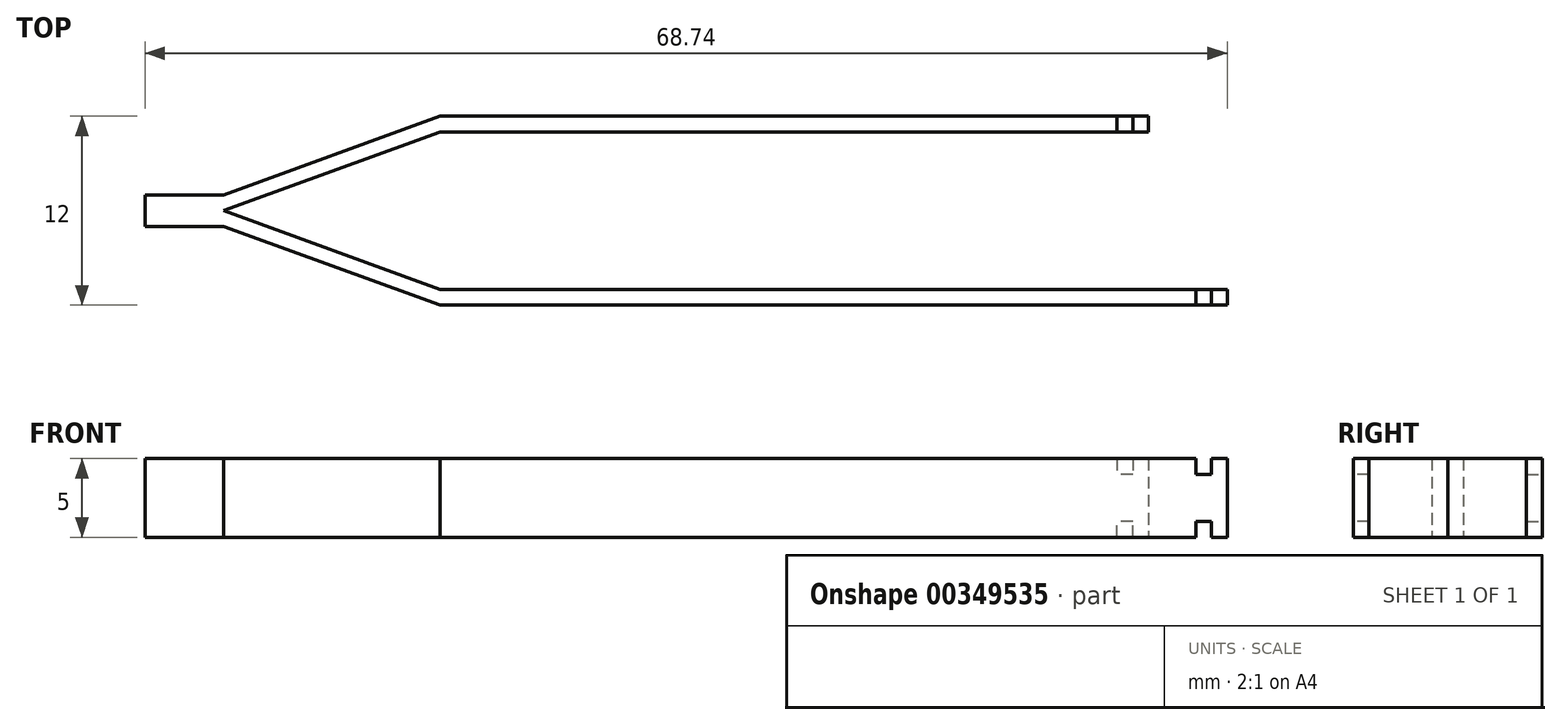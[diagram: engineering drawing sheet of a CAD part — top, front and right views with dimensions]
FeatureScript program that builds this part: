
annotation { "Feature Type Name" : "Feature", "Feature Type Description" : "" }
export const myFeature = defineFeature(function(context is Context, id is Id, definition is map)
    precondition{}
    {
        {
            var Q0;
            Q0=qCreatedBy(makeId("Top.planeOp"),FACE);
            var sketch = newSketch(context, id + "F0", { "sketchPlane" : qUnion([Q0])});
            skLineSegment(sketch, "E0", {"start": v(0, 0) * mm, "end": v(43.22, 0) * mm, "construction": true});
            skLineSegment(sketch, "E1", {"start": v(0, 0) * mm, "end": v(13.74, -5) * mm});
            skLineSegment(sketch, "E2", {"start": v(13.74, -5) * mm, "end": v(63.74, -5) * mm});
            skLineSegment(sketch, "E3", {"start": v(63.74, -5) * mm, "end": v(63.74, -6) * mm});
            skLineSegment(sketch, "E4", {"start": v(63.74, -6) * mm, "end": v(13.74, -6) * mm});
            skLineSegment(sketch, "E5", {"start": v(13.74, -6) * mm, "end": v(0, -1) * mm});
            skLineSegment(sketch, "E6", {"start": v(0, -1) * mm, "end": v(-5, -1) * mm});
            skLineSegment(sketch, "E7", {"start": v(-5, 1) * mm, "end": v(-5, -1) * mm});
            skLineSegment(sketch, "E8", {"start": v(-5, 1) * mm, "end": v(0, 1) * mm});
            skLineSegment(sketch, "E9", {"start": v(0, 1) * mm, "end": v(13.74, 6) * mm});
            skLineSegment(sketch, "E10", {"start": v(13.74, 6) * mm, "end": v(58.74, 6) * mm});
            skLineSegment(sketch, "E11", {"start": v(58.74, 6) * mm, "end": v(58.74, 5) * mm});
            skLineSegment(sketch, "E12", {"start": v(58.74, 5) * mm, "end": v(13.74, 5) * mm});
            skLineSegment(sketch, "E13", {"start": v(13.74, 5) * mm, "end": v(0, 0) * mm});
            skLineSegment(sketch, "E14", {"start": v(13.74, 5) * mm, "end": v(13.74, -5) * mm, "construction": true});
            skSolve(sketch);
        }
        {
            var Q0;
            Q0=makeQuery(id+"F0.imprint","IMPRINT",FACE,{"disambiguationData":[TD([[makeQuery(id+"F0.imprint","IMPRINT",EDGE,{"derivedFrom":sQuery(id+"F0.wireOp",EDGE,"E1")}),-1.0]])]});
            extrude(context, id + "F1", {"entities" : qUnion([Q0]), "depth" : 5 * mm});
        }
        {
            var Q0;
            Q0=makeQuery(id+"F1.opExtrude","SWEPT_FACE",FACE,{"disambiguationData":[OSD([sQuery(id+"F0.wireOp",EDGE,"E10")])]});
            var sketch = newSketch(context, id + "F2", { "sketchPlane" : qUnion([Q0])});
            skLineSegment(sketch, "E15.bottom", {"start": v(-57.74, 5) * mm, "end": v(-56.74, 5) * mm});
            skLineSegment(sketch, "E15.top", {"start": v(-57.74, 4) * mm, "end": v(-56.74, 4) * mm});
            skLineSegment(sketch, "E15.left", {"start": v(-57.74, 5) * mm, "end": v(-57.74, 4) * mm});
            skLineSegment(sketch, "E15.right", {"start": v(-56.74, 5) * mm, "end": v(-56.74, 4) * mm});
            skLineSegment(sketch, "E16", {"start": v(-58.74, 2.5) * mm, "end": v(-53.74, 2.5) * mm, "construction": true});
            skLineSegment(sketch, "E17.MirrorCS", {"start": v(-57.74, 1) * mm, "end": v(-56.74, 1) * mm});
            skLineSegment(sketch, "E18.MirrorCS", {"start": v(-56.74, 0) * mm, "end": v(-56.74, 1) * mm});
            skLineSegment(sketch, "E19.MirrorCS", {"start": v(-57.74, 0) * mm, "end": v(-57.74, 1) * mm});
            skLineSegment(sketch, "E20.MirrorCS", {"start": v(-57.74, 0) * mm, "end": v(-56.74, 0) * mm});
            skSolve(sketch);
        }
        {
            var Q0;
            Q0=makeQuery(id+"F2.imprint","IMPRINT",FACE,{"disambiguationData":[TD([[makeQuery(id+"F2.imprint","IMPRINT",EDGE,{"derivedFrom":sQuery(id+"F2.wireOp",EDGE,"E15.bottom")}),1.0]])]});
            var Q1;
            Q1=makeQuery(id+"F2.imprint","IMPRINT",FACE,{"disambiguationData":[TD([[makeQuery(id+"F2.imprint","IMPRINT",EDGE,{"derivedFrom":sQuery(id+"F2.wireOp",EDGE,"E17.MirrorCS")}),-1.0]])]});
            var Q2;
            Q2=makeQuery(id+"F1.opExtrude","SWEPT_FACE",FACE,{"disambiguationData":[OSD([sQuery(id+"F0.wireOp",EDGE,"E12")])]});
            extrude(context, id + "F3", {"entities" : qUnion([Q0, Q1]), "operationType" : NewBodyOperationType.REMOVE, "endBound" : BoundingType.UP_TO_SURFACE, "oppositeDirection" : true, "endBoundEntityFace" : qUnion([Q2]), "depth" : 25 * mm});
        }
        {
            var Q0;
            Q0=makeQuery(id+"F1.opExtrude","SWEPT_FACE",FACE,{"disambiguationData":[OSD([sQuery(id+"F0.wireOp",EDGE,"E4")])]});
            var sketch = newSketch(context, id + "F4", { "sketchPlane" : qUnion([Q0])});
            skLineSegment(sketch, "E21.bottom", {"start": v(62.74, 5) * mm, "end": v(61.74, 5) * mm});
            skLineSegment(sketch, "E21.top", {"start": v(62.74, 4) * mm, "end": v(61.74, 4) * mm});
            skLineSegment(sketch, "E21.left", {"start": v(62.74, 5) * mm, "end": v(62.74, 4) * mm});
            skLineSegment(sketch, "E21.right", {"start": v(61.74, 5) * mm, "end": v(61.74, 4) * mm});
            skLineSegment(sketch, "E22", {"start": v(63.74, 2.5) * mm, "end": v(58.74, 2.5) * mm, "construction": true});
            skLineSegment(sketch, "E23.MirrorCS", {"start": v(62.74, 1) * mm, "end": v(61.74, 1) * mm});
            skLineSegment(sketch, "E24.MirrorCS", {"start": v(62.74, 0) * mm, "end": v(62.74, 1) * mm});
            skLineSegment(sketch, "E25.MirrorCS", {"start": v(61.74, 0) * mm, "end": v(61.74, 1) * mm});
            skLineSegment(sketch, "E26.MirrorCS", {"start": v(62.74, 0) * mm, "end": v(61.74, 0) * mm});
            skSolve(sketch);
        }
        {
            var Q0;
            Q0 = qSketchRegion(id + "F4", true);
            var Q1;
            Q1=makeQuery(id+"F1.opExtrude","SWEPT_FACE",FACE,{"disambiguationData":[OSD([sQuery(id+"F0.wireOp",EDGE,"E2")])]});
            extrude(context, id + "F5", {"entities" : qUnion([Q0]), "operationType" : NewBodyOperationType.REMOVE, "endBound" : BoundingType.UP_TO_SURFACE, "oppositeDirection" : true, "endBoundEntityFace" : qUnion([Q1]), "depth" : 25 * mm});
        }
    });
